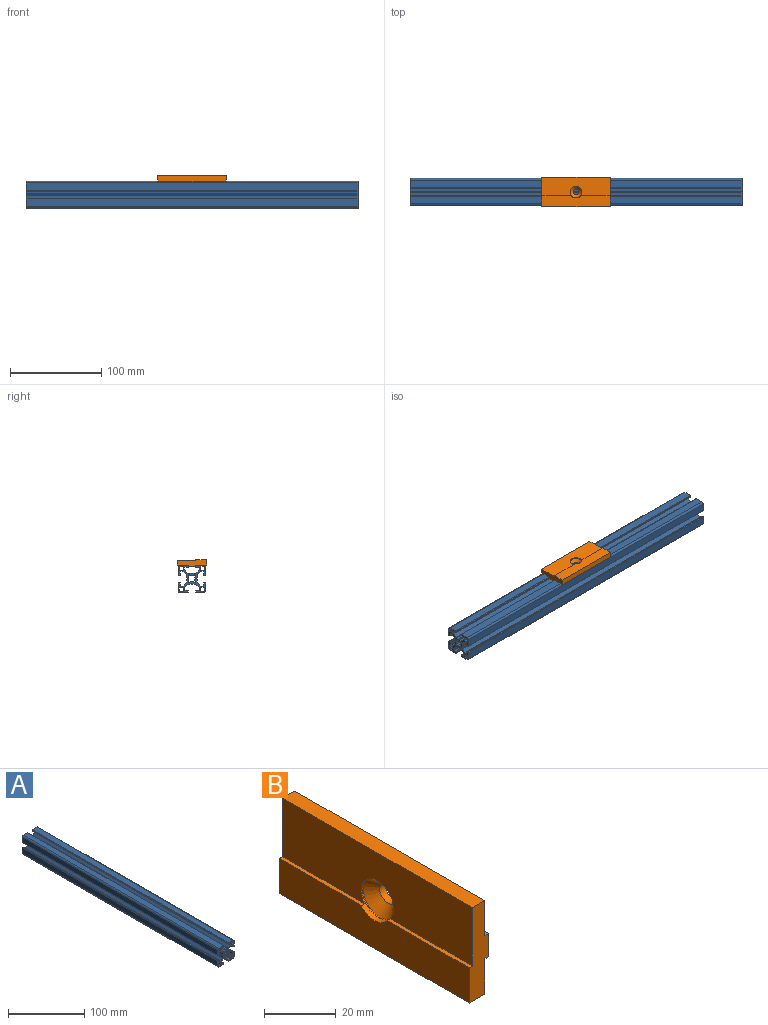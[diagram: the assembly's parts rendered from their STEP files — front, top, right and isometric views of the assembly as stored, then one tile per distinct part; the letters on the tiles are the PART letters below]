
ASSEMBLY  parts=2 mates=1
PART A: 150 faces, bbox 30x363.7x30 mm
  f0: cylinder r=0.38mm len=363.68mm, axis (0,1,0), area 217.7mm2, adj f1,f9,f148,f149
  f1: plane 30x30mm, normal (0,1,0), area 312.7mm2, adj f0,f2,f3,f4,f5,f6,f7,f8
  f2: cylinder r=2mm len=363.68mm, axis (0,1,0), area 1142.5mm2, adj f1,f3,f9,f11
  f3: plane 363.68x8.49mm, normal (0,0,-1), area 3088.4mm2, adj f1,f2,f4,f9
  f4: cylinder r=0.51mm len=363.68mm, axis (0,1,0), area 290.2mm2, adj f1,f3,f5,f9
  f5: plane 363.68x1.24mm, normal (1,0,0), area 451.3mm2, adj f1,f4,f6,f9
  f6: cylinder r=0.51mm len=363.68mm, axis (0,1,0), area 290.2mm2, adj f1,f5,f7,f9
  f7: plane 363.68x3.23mm, normal (0,0,1), area 1176.2mm2, adj f1,f6,f8,f9
  f8: cylinder r=0.51mm len=363.68mm, axis (0,1,0), area 290.2mm2, adj f1,f7,f9,f102
  f9: plane 30x30mm, normal (0,-1,0), area 312.7mm2, adj f0,f2,f3,f4,f5,f6,f7,f8
  f10: cylinder r=0.51mm len=363.68mm, axis (0,1,0), area 290.2mm2, adj f1,f9,f11,f12
  f11: plane 363.68x8.49mm, normal (-1,0,0), area 3088.4mm2, adj f1,f2,f9,f10
  f12: plane 363.68x1.24mm, normal (0,0,1), area 451.3mm2, adj f1,f9,f10,f13
  f13: cylinder r=0.51mm len=363.68mm, axis (0,1,0), area 290.2mm2, adj f1,f9,f12,f14
  f14: plane 363.68x3.23mm, normal (1,0,0), area 1176.2mm2, adj f1,f9,f13,f15
  f15: cylinder r=0.51mm len=363.68mm, axis (0,1,0), area 290.2mm2, adj f1,f9,f14,f16
  f16: plane 363.68x1.97mm, normal (0,0,1), area 717.2mm2, adj f1,f9,f15,f17
  f17: cylinder r=0.51mm len=363.68mm, axis (0,1,0), area 145.1mm2, adj f1,f9,f16,f18
  f18: plane 363.68x3.92mm, normal (-0.71,0,0.71), area 2016.4mm2, adj f1,f9,f17,f19
  f19: cylinder r=0.51mm len=363.68mm, axis (0,1,0), area 145.1mm2, adj f1,f9,f18,f20
  f20: plane 363.68x2.87mm, normal (-1,0,0), area 1044.7mm2, adj f1,f9,f19,f21
  f21: plane 363.68x0.95mm, normal (-0.88,0,0.47), area 391.7mm2, adj f1,f9,f20,f22
  f22: plane 363.68x0.95mm, normal (-0.88,0,-0.47), area 391.7mm2, adj f1,f9,f21,f23
  f23: plane 363.68x2.87mm, normal (-1,0,0), area 1044.2mm2, adj f1,f9,f22,f24
  f24: cylinder r=0.51mm len=363.68mm, axis (0,1,0), area 145.1mm2, adj f1,f9,f23,f25
  f25: plane 363.68x3.92mm, normal (-0.71,0,-0.71), area 2017mm2, adj f1,f9,f24,f26
  f26: cylinder r=0.51mm len=363.68mm, axis (0,1,0), area 145.1mm2, adj f1,f9,f25,f27
  f27: plane 363.68x1.97mm, normal (0,0,-1), area 716.8mm2, adj f1,f9,f26,f28
  f28: cylinder r=0.51mm len=363.68mm, axis (0,1,0), area 290.2mm2, adj f1,f9,f27,f29
  f29: plane 363.68x3.23mm, normal (1,0,0), area 1176.2mm2, adj f1,f9,f28,f30
  f30: cylinder r=0.51mm len=363.68mm, axis (0,1,0), area 290.2mm2, adj f1,f9,f29,f31
  f31: plane 363.68x1.24mm, normal (0,0,-1), area 451.3mm2, adj f1,f9,f30,f32
  f32: cylinder r=0.51mm len=363.68mm, axis (0,1,0), area 290.2mm2, adj f1,f9,f31,f33
  f33: plane 363.68x8.49mm, normal (-1,0,0), area 3088.4mm2, adj f1,f9,f32,f34
  f34: cylinder r=2mm len=363.68mm, axis (0,1,0), area 1142.5mm2, adj f1,f9,f33,f35
  f35: plane 363.68x8.49mm, normal (0,0,1), area 3088.4mm2, adj f1,f9,f34,f36
  f36: cylinder r=0.51mm len=363.68mm, axis (0,1,0), area 290.2mm2, adj f1,f9,f35,f37
  f37: plane 363.68x1.24mm, normal (1,0,0), area 451.3mm2, adj f1,f9,f36,f38
  f38: cylinder r=0.51mm len=363.68mm, axis (0,1,0), area 290.2mm2, adj f1,f9,f37,f39
  f39: plane 363.68x3.23mm, normal (0,0,-1), area 1176.2mm2, adj f1,f9,f38,f40
  f40: cylinder r=0.51mm len=363.68mm, axis (0,1,0), area 290.2mm2, adj f1,f9,f39,f41
  f41: plane 363.68x1.97mm, normal (1,0,0), area 717.2mm2, adj f1,f9,f40,f42
  f42: cylinder r=0.51mm len=363.68mm, axis (0,1,0), area 145.1mm2, adj f1,f9,f41,f43
  f43: plane 363.68x3.92mm, normal (0.71,0,0.71), area 2016.4mm2, adj f1,f9,f42,f44
  f44: cylinder r=0.51mm len=363.68mm, axis (0,1,0), area 145.1mm2, adj f1,f9,f43,f45
  f45: plane 363.68x2.87mm, normal (0,0,1), area 1044.7mm2, adj f1,f9,f44,f46
  f46: plane 363.68x0.95mm, normal (0.47,0,0.88), area 391.7mm2, adj f1,f9,f45,f47
  f47: plane 363.68x0.95mm, normal (-0.47,0,0.88), area 391.7mm2, adj f1,f9,f46,f48
  f48: plane 363.68x2.87mm, normal (0,0,1), area 1044.2mm2, adj f1,f9,f47,f49
  f49: cylinder r=0.51mm len=363.68mm, axis (0,1,0), area 145.1mm2, adj f1,f9,f48,f50
  f50: plane 363.68x3.92mm, normal (-0.71,0,0.71), area 2017mm2, adj f1,f9,f49,f51
  f51: cylinder r=0.51mm len=363.68mm, axis (0,1,0), area 145.1mm2, adj f1,f9,f50,f52
  f52: plane 363.68x1.97mm, normal (-1,0,0), area 716.8mm2, adj f1,f9,f51,f53
  f53: cylinder r=0.51mm len=363.68mm, axis (0,1,0), area 290.2mm2, adj f1,f9,f52,f54
  f54: plane 363.68x3.23mm, normal (0,0,-1), area 1176.2mm2, adj f1,f9,f53,f55
  f55: cylinder r=0.51mm len=363.68mm, axis (0,1,0), area 290.2mm2, adj f1,f9,f54,f56
  f56: plane 363.68x1.24mm, normal (-1,0,0), area 451.3mm2, adj f1,f9,f55,f57
  f57: cylinder r=0.51mm len=363.68mm, axis (0,1,0), area 290.2mm2, adj f1,f9,f56,f58
  f58: plane 363.68x8.49mm, normal (0,0,1), area 3088.4mm2, adj f1,f9,f57,f59
  f59: cylinder r=2mm len=363.68mm, axis (0,1,0), area 1142.5mm2, adj f1,f9,f58,f60
  f60: plane 363.68x8.49mm, normal (1,0,0), area 3088.4mm2, adj f1,f9,f59,f61
  f61: cylinder r=0.51mm len=363.68mm, axis (0,1,0), area 290.2mm2, adj f1,f9,f60,f62
  f62: plane 363.68x1.24mm, normal (0,0,-1), area 451.3mm2, adj f1,f9,f61,f63
  f63: cylinder r=0.51mm len=363.68mm, axis (0,1,0), area 290.2mm2, adj f1,f9,f62,f64
  f64: plane 363.68x3.23mm, normal (-1,0,0), area 1176.2mm2, adj f1,f9,f63,f65
  f65: cylinder r=0.51mm len=363.68mm, axis (0,1,0), area 290.2mm2, adj f1,f9,f64,f66
  f66: plane 363.68x1.97mm, normal (0,0,-1), area 717.2mm2, adj f1,f9,f65,f67
  f67: cylinder r=0.51mm len=363.68mm, axis (0,1,0), area 145.1mm2, adj f1,f9,f66,f68
  f68: plane 363.68x3.92mm, normal (0.71,0,-0.71), area 2016.4mm2, adj f1,f9,f67,f69
  f69: cylinder r=0.51mm len=363.68mm, axis (0,1,0), area 145.1mm2, adj f1,f9,f68,f70
  f70: plane 363.68x2.87mm, normal (1,0,0), area 1044.7mm2, adj f1,f9,f69,f71
  f71: plane 363.68x0.95mm, normal (0.88,0,-0.47), area 391.7mm2, adj f1,f9,f70,f72
  f72: plane 363.68x0.95mm, normal (0.88,0,0.47), area 391.7mm2, adj f1,f9,f71,f73
  f73: plane 363.68x2.87mm, normal (1,0,0), area 1044.2mm2, adj f1,f9,f72,f74
  f74: cylinder r=0.51mm len=363.68mm, axis (0,1,0), area 145.1mm2, adj f1,f9,f73,f75
  f75: plane 363.68x3.92mm, normal (0.71,0,0.71), area 2017mm2, adj f1,f9,f74,f76
  f76: cylinder r=0.51mm len=363.68mm, axis (0,1,0), area 145.1mm2, adj f1,f9,f75,f77
  f77: plane 363.68x1.97mm, normal (0,0,1), area 716.8mm2, adj f1,f9,f76,f78
  f78: cylinder r=0.51mm len=363.68mm, axis (0,1,0), area 290.2mm2, adj f1,f9,f77,f79
  f79: plane 363.68x3.23mm, normal (-1,0,0), area 1176.2mm2, adj f1,f9,f78,f80
  f80: cylinder r=0.51mm len=363.68mm, axis (0,1,0), area 290.2mm2, adj f1,f9,f79,f81
  f81: plane 363.68x1.24mm, normal (0,0,1), area 451.3mm2, adj f1,f9,f80,f82
  f82: cylinder r=0.51mm len=363.68mm, axis (0,1,0), area 290.2mm2, adj f1,f9,f81,f83
  f83: plane 363.68x8.49mm, normal (1,0,0), area 3088.4mm2, adj f1,f9,f82,f84
  f84: cylinder r=2mm len=363.68mm, axis (0,1,0), area 1142.5mm2, adj f1,f9,f83,f85
  f85: plane 363.68x8.49mm, normal (0,0,-1), area 3088.4mm2, adj f1,f9,f84,f86
  f86: cylinder r=0.51mm len=363.68mm, axis (0,1,0), area 290.2mm2, adj f1,f9,f85,f87
  f87: plane 363.68x1.24mm, normal (-1,0,0), area 451.3mm2, adj f1,f9,f86,f88
  f88: cylinder r=0.51mm len=363.68mm, axis (0,1,0), area 290.2mm2, adj f1,f9,f87,f89
  f89: plane 363.68x3.23mm, normal (0,0,1), area 1176.2mm2, adj f1,f9,f88,f90
  f90: cylinder r=0.51mm len=363.68mm, axis (0,1,0), area 290.2mm2, adj f1,f9,f89,f91
  f91: plane 363.68x1.97mm, normal (-1,0,0), area 717.2mm2, adj f1,f9,f90,f92
  f92: cylinder r=0.51mm len=363.68mm, axis (0,1,0), area 145.1mm2, adj f1,f9,f91,f93
  f93: plane 363.68x3.92mm, normal (-0.71,0,-0.71), area 2016.4mm2, adj f1,f9,f92,f94
  f94: cylinder r=0.51mm len=363.68mm, axis (0,1,0), area 145.1mm2, adj f1,f9,f93,f95
  f95: plane 363.68x2.87mm, normal (0,0,-1), area 1044.7mm2, adj f1,f9,f94,f96
  f96: plane 363.68x0.95mm, normal (-0.47,0,-0.88), area 391.7mm2, adj f1,f9,f95,f97
  f97: plane 363.68x0.95mm, normal (0.47,0,-0.88), area 391.7mm2, adj f1,f9,f96,f98
  f98: plane 363.68x2.87mm, normal (0,0,-1), area 1044.2mm2, adj f1,f9,f97,f99
  f99: cylinder r=0.51mm len=363.68mm, axis (0,1,0), area 145.1mm2, adj f1,f9,f98,f100
  f100: plane 363.68x3.92mm, normal (0.71,0,-0.71), area 2017mm2, adj f1,f9,f99,f101
  f101: cylinder r=0.51mm len=363.68mm, axis (0,1,0), area 145.1mm2, adj f1,f9,f100,f102
  f102: plane 363.68x1.97mm, normal (1,0,0), area 716.8mm2, adj f1,f8,f9,f101
  f103: cylinder r=0.38mm len=363.68mm, axis (0,1,0), area 217.7mm2, adj f1,f9,f104,f110
  f104: plane 363.68x2.82mm, normal (0,0,1), area 1025.2mm2, adj f1,f9,f103,f105
  f105: cylinder r=1mm len=363.68mm, axis (0,1,0), area 571.3mm2, adj f1,f9,f104,f106
  f106: plane 363.68x2.82mm, normal (-1,0,0), area 1025.2mm2, adj f1,f9,f105,f107
  f107: cylinder r=0.38mm len=363.68mm, axis (0,1,0), area 217.7mm2, adj f1,f9,f106,f108
  f108: plane 363.68x3.44mm, normal (0,0,-1), area 1250.3mm2, adj f1,f9,f107,f109
  f109: cylinder r=0.38mm len=363.68mm, axis (0,1,0), area 217.7mm2, adj f1,f9,f108,f110
  f110: plane 363.68x3.44mm, normal (1,0,0), area 1250.3mm2, adj f1,f9,f103,f109
  f111: cylinder r=0.38mm len=363.68mm, axis (0,1,0), area 217.7mm2, adj f1,f9,f112,f118
  f112: plane 363.68x3.44mm, normal (0,0,1), area 1250.3mm2, adj f1,f9,f111,f113
  f113: cylinder r=0.38mm len=363.68mm, axis (0,1,0), area 217.7mm2, adj f1,f9,f112,f114
  f114: plane 363.68x2.82mm, normal (-1,0,0), area 1025.2mm2, adj f1,f9,f113,f115
  f115: cylinder r=1mm len=363.68mm, axis (0,1,0), area 571.3mm2, adj f1,f9,f114,f116
  f116: plane 363.68x2.82mm, normal (0,0,-1), area 1025.2mm2, adj f1,f9,f115,f117
  f117: cylinder r=0.38mm len=363.68mm, axis (0,1,0), area 217.7mm2, adj f1,f9,f116,f118
  f118: plane 363.68x3.44mm, normal (1,0,0), area 1250.3mm2, adj f1,f9,f111,f117
  f119: cylinder r=1.07mm len=363.68mm, axis (0,1,0), area 1100.5mm2, adj f1,f9,f120,f134
  f120: plane 363.68x1.02mm, normal (-0.62,0,0.78), area 474.2mm2, adj f1,f9,f119,f121
  f121: cylinder r=3.53mm len=363.68mm, axis (0,1,0), area 1122.2mm2, adj f1,f9,f120,f122
  f122: plane 363.68x1.02mm, normal (0.62,0,0.78), area 474.2mm2, adj f1,f9,f121,f123
  f123: cylinder r=1.07mm len=363.68mm, axis (0,1,0), area 1100.5mm2, adj f1,f9,f122,f124
  f124: plane 363.68x1.02mm, normal (-0.78,0,-0.62), area 474.2mm2, adj f1,f9,f123,f125
  f125: cylinder r=3.53mm len=363.68mm, axis (0,1,0), area 1122.2mm2, adj f1,f9,f124,f126
  f126: plane 363.68x1.02mm, normal (-0.78,0,0.62), area 474.2mm2, adj f1,f9,f125,f127
  f127: cylinder r=1.07mm len=363.68mm, axis (0,1,0), area 1100.5mm2, adj f1,f9,f126,f128
  f128: plane 363.68x1.02mm, normal (0.62,0,-0.78), area 474.2mm2, adj f1,f9,f127,f129
  f129: cylinder r=3.53mm len=363.68mm, axis (0,1,0), area 1122.2mm2, adj f1,f9,f128,f130
  f130: plane 363.68x1.02mm, normal (-0.62,0,-0.78), area 474.2mm2, adj f1,f9,f129,f131
  f131: cylinder r=1.07mm len=363.68mm, axis (0,1,0), area 1100.5mm2, adj f1,f9,f130,f132
  f132: plane 363.68x1.02mm, normal (0.78,0,0.62), area 474.2mm2, adj f1,f9,f131,f133
  f133: cylinder r=3.53mm len=363.68mm, axis (0,1,0), area 1122.2mm2, adj f1,f9,f132,f134
  f134: plane 363.68x1.02mm, normal (0.78,0,-0.62), area 474.2mm2, adj f1,f9,f119,f133
  f135: cylinder r=0.38mm len=363.68mm, axis (0,1,0), area 217.7mm2, adj f1,f9,f136,f142
  f136: plane 363.68x3.44mm, normal (0,0,1), area 1250.3mm2, adj f1,f9,f135,f137
  f137: cylinder r=0.38mm len=363.68mm, axis (0,1,0), area 217.7mm2, adj f1,f9,f136,f138
  f138: plane 363.68x3.44mm, normal (-1,0,0), area 1250.3mm2, adj f1,f9,f137,f139
  f139: cylinder r=0.38mm len=363.68mm, axis (0,1,0), area 217.7mm2, adj f1,f9,f138,f140
  f140: plane 363.68x2.82mm, normal (0,0,-1), area 1025.2mm2, adj f1,f9,f139,f141
  f141: cylinder r=1mm len=363.68mm, axis (0,1,0), area 571.3mm2, adj f1,f9,f140,f142
  f142: plane 363.68x2.82mm, normal (1,0,0), area 1025.2mm2, adj f1,f9,f135,f141
  f143: cylinder r=1mm len=363.68mm, axis (0,1,0), area 571.3mm2, adj f1,f9,f144,f149
  f144: plane 363.68x2.82mm, normal (0,0,1), area 1025.2mm2, adj f1,f9,f143,f145
  f145: cylinder r=0.38mm len=363.68mm, axis (0,1,0), area 217.7mm2, adj f1,f9,f144,f146
  f146: plane 363.68x3.44mm, normal (-1,0,0), area 1250.3mm2, adj f1,f9,f145,f147
  f147: cylinder r=0.38mm len=363.68mm, axis (0,1,0), area 217.7mm2, adj f1,f9,f146,f148
  f148: plane 363.68x3.44mm, normal (0,0,-1), area 1250.3mm2, adj f0,f1,f9,f147
  f149: plane 363.68x2.82mm, normal (1,0,0), area 1025.2mm2, adj f0,f1,f9,f143
PART B: 17 faces, bbox 7.7x74.6x31.8 mm
  f0: plane 74.6x6.1mm, normal (0,0,-1), area 454.8mm2, adj f1,f6,f10,f16
  f1: plane 74.6x11.95mm, normal (1,0,0), area 891.5mm2, adj f0,f2,f10,f16
  f2: plane 74.6x1.56mm, normal (0,0,-1), area 116.5mm2, adj f1,f8,f10,f16
  f3: plane 74.6x1.56mm, normal (0,0,1), area 116.5mm2, adj f4,f8,f10,f16
  f4: plane 74.6x11.95mm, normal (1,0,0), area 891.5mm2, adj f3,f5,f10,f16
  f5: plane 74.6x4.85mm, normal (0,0,1), area 361.9mm2, adj f4,f7,f10,f16
  f6: plane 74.6x11.95mm, normal (-1,0,0), area 873.8mm2, adj f0,f9,f10,f11,f15,f16
  f7: plane 74.6x19.85mm, normal (-1,0,0), area 1368.2mm2, adj f5,f9,f10,f11,f15,f16
  f8: plane 74.6x7.9mm, normal (1,0,0), area 556.8mm2, adj f2,f3,f10,f12,f16
  f9: plane 32.21x1.24mm, normal (0,0,1), area 40.1mm2, adj f6,f7,f11,f16
  f10: plane 31.8x7.66mm, normal (0,1,0), area 181.5mm2, adj f0,f1,f2,f3,f4,f5,f6,f7
  f11: cylinder r=6.44mm len=12.88mm, axis (1,0,0), area 33.1mm2, adj f6,f7,f9,f14,f15
  f12: cylinder r=3.22mm len=6.44mm, axis (1,0,0), area 46.6mm2, adj f8,f13
  f13: cone r=3.22mm half-angle=45deg, axis (-1,0,0), area 137.6mm2, adj f12,f14
  f14: cylinder r=6.44mm len=12.87mm, axis (1,0,0), area 17.5mm2, adj f11,f13
  f15: plane 32.22x1.24mm, normal (0,0,1), area 40.1mm2, adj f6,f7,f10,f11
  f16: plane 31.8x7.66mm, normal (0,-1,0), area 181.5mm2, adj f0,f1,f2,f3,f4,f5,f6,f7
PLACE A rot(axis=(0,0,-1),90deg) t=(475.53,-415.92,-1072.89)mm
PLACE B rot(axis=(-0.58,0.58,0.58),120deg) t=(413.69,-416.02,-2.65)mm
MATE planar B.f1 <-> A.f58  axis (0,0,-1) through (393.68,-425.94,-4.85)mm
